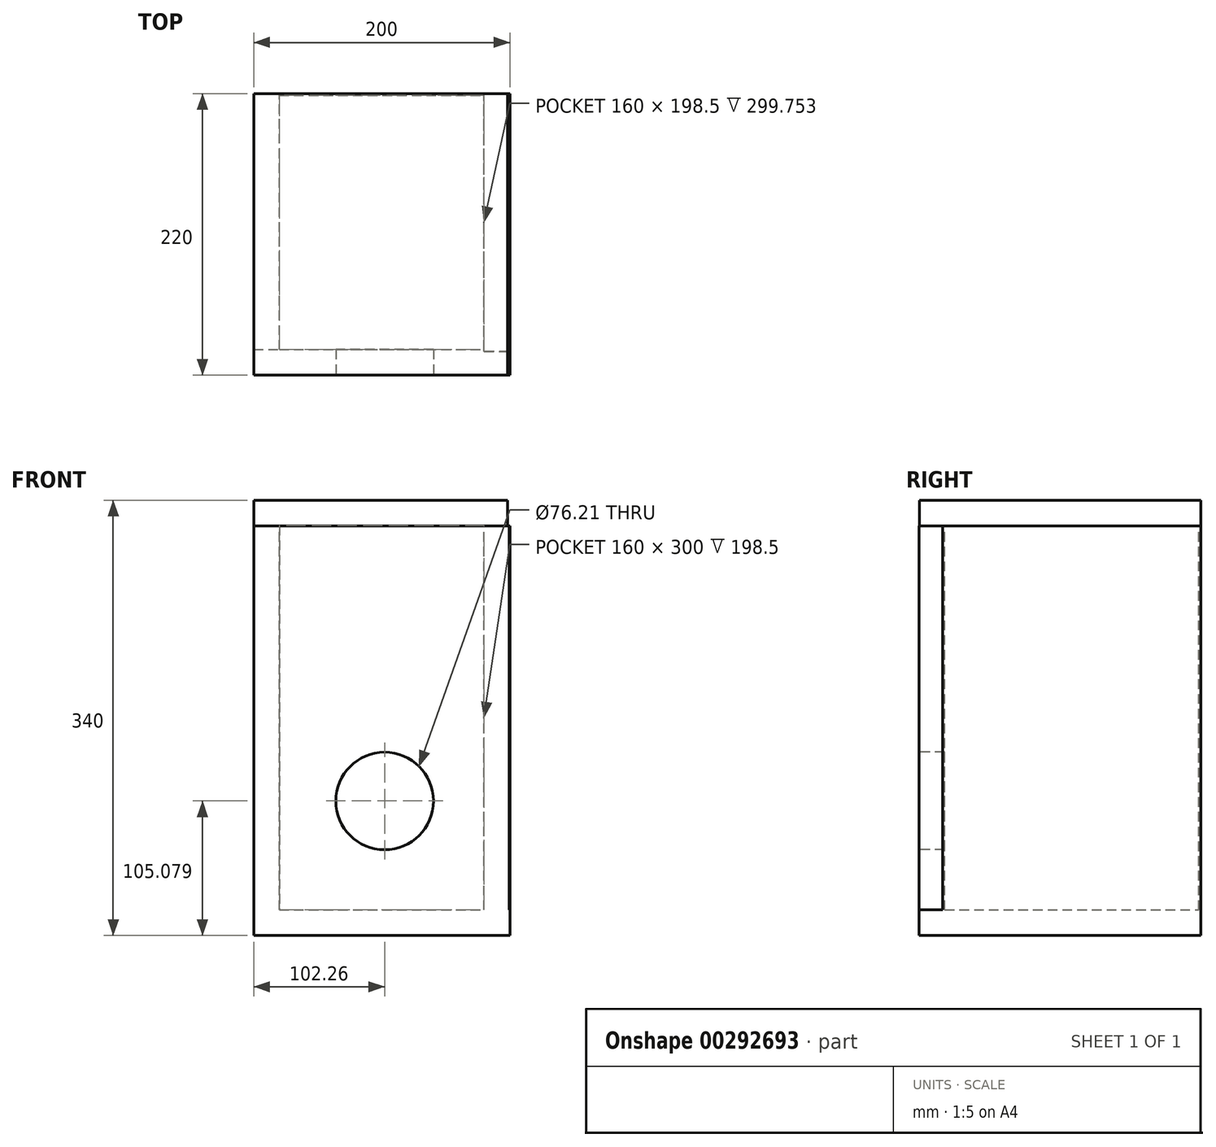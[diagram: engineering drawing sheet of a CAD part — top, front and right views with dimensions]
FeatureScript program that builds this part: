
annotation { "Feature Type Name" : "Feature", "Feature Type Description" : "" }
export const myFeature = defineFeature(function(context is Context, id is Id, definition is map)
    precondition{}
    {
        {
            var Q0;
            Q0=qCreatedBy(makeId("Front.planeOp"),FACE);
            var sketch = newSketch(context, id + "F0", { "sketchPlane" : qUnion([Q0])});
            skLineSegment(sketch, "E0.bottom", {"start": v(0, 0) * mm, "end": v(200, 0) * mm});
            skLineSegment(sketch, "E0.top", {"start": v(0, 300) * mm, "end": v(200, 300) * mm});
            skLineSegment(sketch, "E0.left", {"start": v(0, 0) * mm, "end": v(0, 300) * mm});
            skLineSegment(sketch, "E0.right", {"start": v(200, 0) * mm, "end": v(200, 300) * mm});
            skSolve(sketch);
        }
        {
            var Q0;
            Q0 = qSketchRegion(id + "F0", true);
            extrude(context, id + "F1", {"entities" : qUnion([Q0]), "depth" : 1.5 * mm});
        }
        {
            var Q0;
            Q0=qCreatedBy(makeId("Front.planeOp"),FACE);
            var sketch = newSketch(context, id + "F2", { "sketchPlane" : qUnion([Q0])});
            skLineSegment(sketch, "E1.bottom", {"start": v(0, 0) * mm, "end": v(20, 0) * mm});
            skLineSegment(sketch, "E1.top", {"start": v(0, 300) * mm, "end": v(20, 300) * mm});
            skLineSegment(sketch, "E1.left", {"start": v(0, 0) * mm, "end": v(0, 300) * mm});
            skLineSegment(sketch, "E1.right", {"start": v(20, 0) * mm, "end": v(20, 300) * mm});
            skSolve(sketch);
        }
        {
            var Q0;
            Q0 = qSketchRegion(id + "F2", true);
            extrude(context, id + "F3", {"entities" : qUnion([Q0]), "operationType" : NewBodyOperationType.ADD, "depth" : 200 * mm});
        }
        {
            var Q0;
            Q0=makeQuery(id+"F1.opExtrude","CAP_FACE",FACE,{"disambiguationData":[OSD([sQuery(id+"F0.wireOp",EDGE,"E0.bottom"),sQuery(id+"F0.wireOp",EDGE,"E0.top"),sQuery(id+"F0.wireOp",EDGE,"E0.left"),sQuery(id+"F0.wireOp",EDGE,"E0.right")])],"isStart":false});
            var sketch = newSketch(context, id + "F4", { "sketchPlane" : qUnion([Q0])});
            skLineSegment(sketch, "E2.bottom", {"start": v(200, 0) * mm, "end": v(180, 0) * mm});
            skLineSegment(sketch, "E2.top", {"start": v(200, 300) * mm, "end": v(180, 300) * mm});
            skLineSegment(sketch, "E2.left", {"start": v(200, 0) * mm, "end": v(200, 300) * mm});
            skLineSegment(sketch, "E2.right", {"start": v(180, 0) * mm, "end": v(180, 300) * mm});
            skSolve(sketch);
        }
        {
            var Q0;
            Q0 = qSketchRegion(id + "F4", true);
            extrude(context, id + "F5", {"entities" : qUnion([Q0]), "operationType" : NewBodyOperationType.ADD, "depth" : 200 * mm});
        }
        {
            var Q0;
            Q0=makeQuery(id+"F3.opExtrude","CAP_FACE",FACE,{"disambiguationData":[OSD([sQuery(id+"F2.wireOp",EDGE,"E1.bottom"),sQuery(id+"F2.wireOp",EDGE,"E1.top"),sQuery(id+"F2.wireOp",EDGE,"E1.left"),sQuery(id+"F2.wireOp",EDGE,"E1.right")])],"isStart":false});
            var sketch = newSketch(context, id + "F6", { "sketchPlane" : qUnion([Q0])});
            skLineSegment(sketch, "E3.bottom", {"start": v(0, 0) * mm, "end": v(199.42, 0) * mm});
            skLineSegment(sketch, "E3.top", {"start": v(0, 299.75) * mm, "end": v(199.42, 299.75) * mm});
            skLineSegment(sketch, "E3.left", {"start": v(0, 0) * mm, "end": v(0, 299.75) * mm});
            skLineSegment(sketch, "E3.right", {"start": v(199.42, 0) * mm, "end": v(199.42, 299.75) * mm});
            skSolve(sketch);
        }
        {
            var Q0;
            Q0 = qSketchRegion(id + "F6", true);
            extrude(context, id + "F7", {"entities" : qUnion([Q0]), "operationType" : NewBodyOperationType.ADD, "depth" : 20 * mm});
        }
        {
            var Q0;
            Q0=makeQuery(id+"F5.boolean.opBoolean","MERGE",FACE,{"derivedFrom":[makeQuery(id+"F3.boolean.opBoolean","MERGE",FACE,{"derivedFrom":[makeQuery(id+"F1.opExtrude","SWEPT_FACE",FACE,{"disambiguationData":[OSD([sQuery(id+"F0.wireOp",EDGE,"E0.top")])]}),makeQuery(id+"F3.opExtrude","SWEPT_FACE",FACE,{"disambiguationData":[OSD([sQuery(id+"F2.wireOp",EDGE,"E1.top")])]})]}),makeQuery(id+"F5.opExtrude","SWEPT_FACE",FACE,{"disambiguationData":[OSD([sQuery(id+"F4.wireOp",EDGE,"E2.top")])]})]});
            var sketch = newSketch(context, id + "F8", { "sketchPlane" : qUnion([Q0])});
            skSolve(sketch);
        }
        {
            var Q0;
            {var subQ0=sQuery(id+"F2.wireOp",EDGE,"E1.top");Q0=makeQuery(id+"F8.imprint","IMPRINT",FACE,{"disambiguationData":[TD([[makeQuery(id+"F8.imprint","IMPRINT",EDGE,{"derivedFrom":makeQuery(id+"F3.opExtrude","CAP_EDGE",EDGE,{"disambiguationData":[OSD([subQ0])],"isStart":false})}),1.0]])]});}
            var sketch = newSketch(context, id + "F9", { "sketchPlane" : qUnion([Q0])});
            skLineSegment(sketch, "E4.bottom", {"start": v(0, 0) * mm, "end": v(198.16, 0) * mm});
            skLineSegment(sketch, "E4.top", {"start": v(0, -219.8) * mm, "end": v(198.16, -219.8) * mm});
            skLineSegment(sketch, "E4.left", {"start": v(0, 0) * mm, "end": v(0, -219.8) * mm});
            skLineSegment(sketch, "E4.right", {"start": v(198.16, 0) * mm, "end": v(198.16, -219.8) * mm});
            skSolve(sketch);
        }
        {
            var Q0;
            Q0 = qSketchRegion(id + "F9", true);
            extrude(context, id + "F10", {"entities" : qUnion([Q0]), "operationType" : NewBodyOperationType.ADD, "depth" : 20 * mm});
        }
        {
            var Q0;
            Q0=makeQuery(id+"F7.boolean.opBoolean","MERGE",FACE,{"derivedFrom":[makeQuery(id+"F5.boolean.opBoolean","MERGE",FACE,{"derivedFrom":[makeQuery(id+"F3.boolean.opBoolean","MERGE",FACE,{"derivedFrom":[makeQuery(id+"F1.opExtrude","SWEPT_FACE",FACE,{"disambiguationData":[OSD([sQuery(id+"F0.wireOp",EDGE,"E0.bottom")])]}),makeQuery(id+"F3.opExtrude","SWEPT_FACE",FACE,{"disambiguationData":[OSD([sQuery(id+"F2.wireOp",EDGE,"E1.bottom")])]})]}),makeQuery(id+"F5.opExtrude","SWEPT_FACE",FACE,{"disambiguationData":[OSD([sQuery(id+"F4.wireOp",EDGE,"E2.bottom")])]})]}),makeQuery(id+"F7.opExtrude","SWEPT_FACE",FACE,{"disambiguationData":[OSD([sQuery(id+"F6.wireOp",EDGE,"E3.bottom")])]})]});
            var sketch = newSketch(context, id + "F11", { "sketchPlane" : qUnion([Q0])});
            skLineSegment(sketch, "E5.bottom", {"start": v(0, 220) * mm, "end": v(200, 220) * mm});
            skLineSegment(sketch, "E5.top", {"start": v(0, 0) * mm, "end": v(200, 0) * mm});
            skLineSegment(sketch, "E5.left", {"start": v(0, 220) * mm, "end": v(0, 0) * mm});
            skLineSegment(sketch, "E5.right", {"start": v(200, 220) * mm, "end": v(200, 0) * mm});
            skSolve(sketch);
        }
        {
            var Q0;
            Q0 = qSketchRegion(id + "F11", true);
            extrude(context, id + "F12", {"entities" : qUnion([Q0]), "operationType" : NewBodyOperationType.ADD, "depth" : 20 * mm});
        }
        {
            var Q0;
            Q0=makeQuery(id+"F12.boolean.opBoolean","MERGE",FACE,{"derivedFrom":[makeQuery(id+"F7.opExtrude","CAP_FACE",FACE,{"disambiguationData":[OSD([sQuery(id+"F6.wireOp",EDGE,"E3.bottom"),sQuery(id+"F6.wireOp",EDGE,"E3.top"),sQuery(id+"F6.wireOp",EDGE,"E3.left"),sQuery(id+"F6.wireOp",EDGE,"E3.right")])],"isStart":false}),makeQuery(id+"F12.opExtrude","SWEPT_FACE",FACE,{"disambiguationData":[OSD([sQuery(id+"F11.wireOp",EDGE,"E5.bottom")])]})]});
            var sketch = newSketch(context, id + "F13", { "sketchPlane" : qUnion([Q0])});
            skCircle(sketch, "E6", {"center": v(102.26, 85.08) * mm, "radius": 38.1 * mm});
            skSolve(sketch);
        }
        {
            var Q0;
            Q0 = qSketchRegion(id + "F13", true);
            extrude(context, id + "F14", {"entities" : qUnion([Q0]), "operationType" : NewBodyOperationType.REMOVE, "oppositeDirection" : true, "depth" : 20 * mm});
        }
    });
